# Revit family: Digital_Media-Honeywell-Battery-581730(31)
name_source: partatom
category: Electrical Equipment
revit_build: Autodesk Revit 2017 (Build: 20160225_1515(x64)
units: mm (PartAtom-declared; Revit-internal decimal feet)

## family parameters
Cut with Voids When Loaded = No
Host = Face
OmniClass Number = 23.85.50.00
OmniClass Title = Communication Systems
Part Type = Equipment Switch
Room Calculation Point = No
Round Connector Dimension = Use Diameter
Shared = No

## types (2) — shared parameters
Apparent Load = 12 VA
Finish = Plastic -Honeywell - Yellow
Frequency = 0 Hz
Load Sub-Classification = No
Manufacturer = Honeywell International
Manufacturer Fax Number = 02131/40615-606
Number of Poles = 1
Power Factor = 1
Product Documentation Link = https://www.esser-systems.com
Product Name = Emergency battery
Product Page URL = https://www.esser-systems.com
URL = www.esser-systems.com
Utility = No
Version = 2017 - v1.0a
Watts = 0 W
zero-valued in all types: Default Elevation

## per-type parameters (varying)
| type | Constraints | Description | Height | Length | Model | Weight | Width |
| Battery 12 V / 105 Ah - 581730 | 1 | Battery for emergency power supply 12 V / 105 Ah | 236 mm | 502 mm  [stored 1.64698 ft] | 581730 | 32.50 kgf | 111 mm |
| Battery 12 V / 150 Ah - 581731 | 2 | Battery for emergency power supply 12 V / 150 Ah | 288 mm | 552 mm | 581731 | 49.50 kgf | 110 mm |

note: [stored X ft] marks values corroborated as IEEE doubles in the binary element streams (Revit-internal decimal feet)

## geometry (parser evidence)
native form markers: Sweep x2
no freeform markers — native parametric forms only
